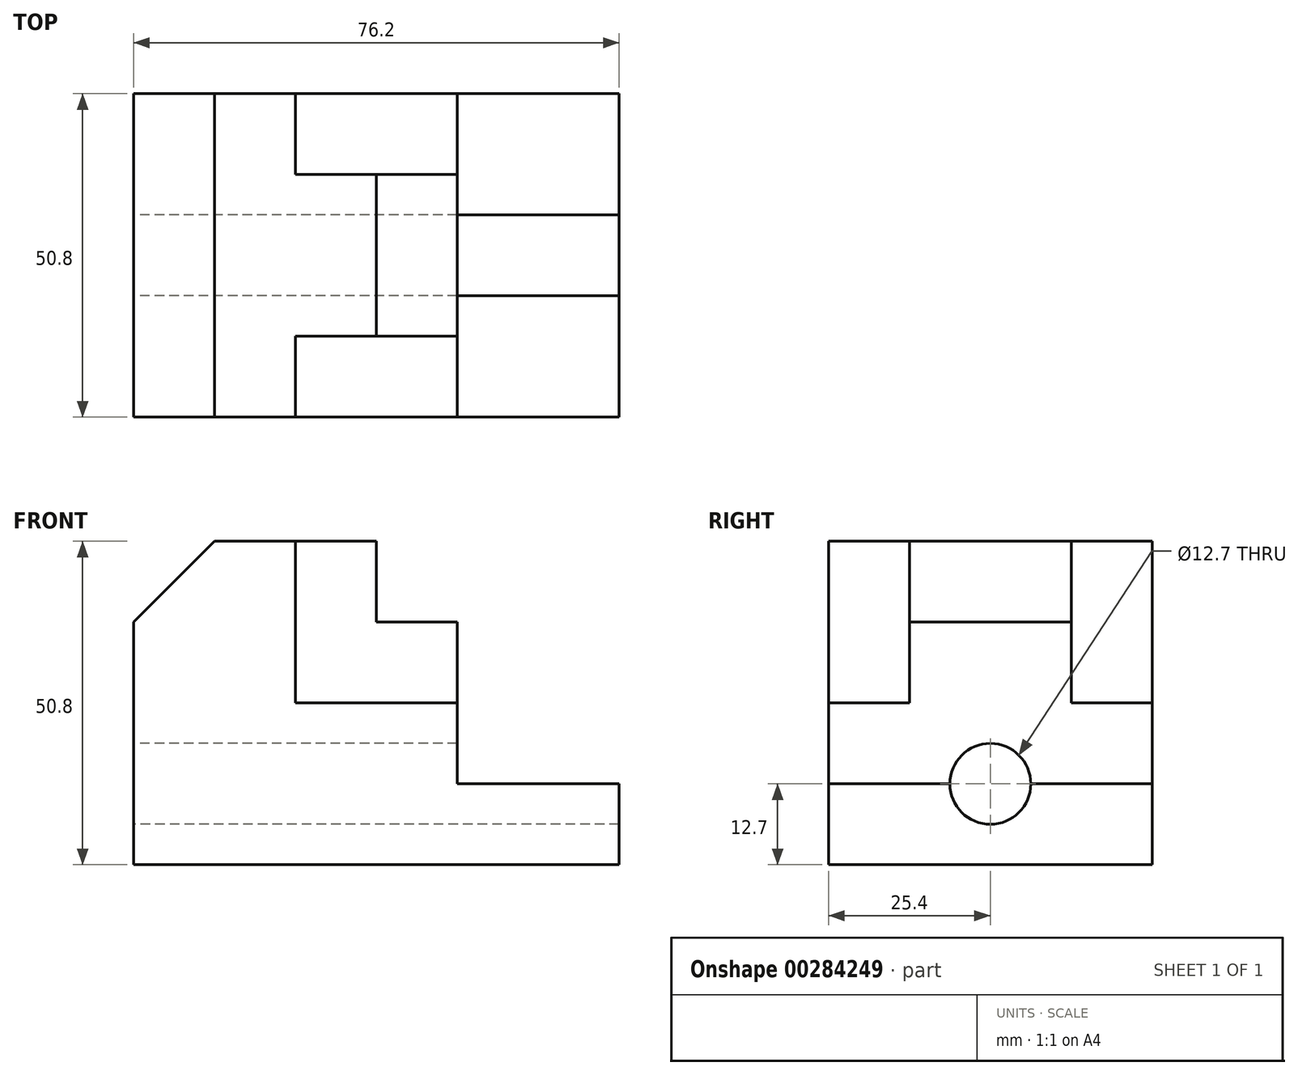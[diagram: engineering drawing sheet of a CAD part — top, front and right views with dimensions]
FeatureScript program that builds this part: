
annotation { "Feature Type Name" : "Feature", "Feature Type Description" : "" }
export const myFeature = defineFeature(function(context is Context, id is Id, definition is map)
    precondition{}
    {
        {
            var Q0;
            Q0=qCreatedBy(makeId("Front.planeOp"),FACE);
            var sketch = newSketch(context, id + "F0", { "sketchPlane" : qUnion([Q0])});
            skLineSegment(sketch, "E0.bottom", {"start": v(0, 0) * mm, "end": v(76.2, 0) * mm});
            skLineSegment(sketch, "E0.top", {"start": v(0, 12.7) * mm, "end": v(76.2, 12.7) * mm});
            skLineSegment(sketch, "E0.left", {"start": v(0, 0) * mm, "end": v(0, 12.7) * mm});
            skLineSegment(sketch, "E0.right", {"start": v(76.2, 0) * mm, "end": v(76.2, 12.7) * mm});
            skLineSegment(sketch, "E1.bottom", {"start": v(0, 12.7) * mm, "end": v(50.8, 12.7) * mm});
            skLineSegment(sketch, "E1.top", {"start": v(0, 25.4) * mm, "end": v(50.8, 25.4) * mm});
            skLineSegment(sketch, "E1.left", {"start": v(0, 12.7) * mm, "end": v(0, 25.4) * mm});
            skLineSegment(sketch, "E1.right", {"start": v(50.8, 12.7) * mm, "end": v(50.8, 25.4) * mm});
            skLineSegment(sketch, "E2", {"start": v(0, 25.4) * mm, "end": v(25.4, 25.4) * mm});
            skLineSegment(sketch, "E3", {"start": v(25.4, 25.4) * mm, "end": v(25.4, 50.8) * mm});
            skLineSegment(sketch, "E4", {"start": v(25.4, 50.8) * mm, "end": v(12.7, 50.8) * mm});
            skLineSegment(sketch, "E5", {"start": v(0, 25.4) * mm, "end": v(0, 38.1) * mm});
            skLineSegment(sketch, "E6", {"start": v(0, 38.1) * mm, "end": v(12.7, 50.8) * mm});
            skSolve(sketch);
        }
        {
            var Q0;
            Q0 = qSketchRegion(id + "F0", true);
            extrude(context, id + "F1", {"entities" : qUnion([Q0]), "endBound" : BoundingType.SYMMETRIC, "depth" : 50.8 * mm});
        }
        {
            var Q0;
            Q0=qCreatedBy(makeId("Right.planeOp"),FACE);
            var sketch = newSketch(context, id + "F2", { "sketchPlane" : qUnion([Q0])});
            skCircle(sketch, "E7", {"center": v(0, 12.7) * mm, "radius": 6.35 * mm});
            skSolve(sketch);
        }
        {
            var Q0;
            Q0 = qSketchRegion(id + "F2", true);
            extrude(context, id + "F3", {"entities" : qUnion([Q0]), "operationType" : NewBodyOperationType.REMOVE, "endBound" : BoundingType.THROUGH_ALL, "depth" : 25.4 * mm});
        }
        {
            var Q0;
            Q0=qCreatedBy(makeId("Front.planeOp"),FACE);
            var sketch = newSketch(context, id + "F4", { "sketchPlane" : qUnion([Q0])});
            skLineSegment(sketch, "E8", {"start": v(25.4, 50.8) * mm, "end": v(38.1, 50.8) * mm});
            skLineSegment(sketch, "E9", {"start": v(38.1, 50.8) * mm, "end": v(38.1, 38.1) * mm});
            skLineSegment(sketch, "E10", {"start": v(38.1, 38.1) * mm, "end": v(50.8, 38.1) * mm});
            skLineSegment(sketch, "E11", {"start": v(50.8, 38.1) * mm, "end": v(50.8, 25.4) * mm});
            skLineSegment(sketch, "E12", {"start": v(50.8, 25.4) * mm, "end": v(25.4, 25.4) * mm});
            skLineSegment(sketch, "E13", {"start": v(25.4, 25.4) * mm, "end": v(25.4, 50.8) * mm});
            skSolve(sketch);
        }
        {
            var Q0;
            Q0 = qSketchRegion(id + "F4", true);
            extrude(context, id + "F5", {"entities" : qUnion([Q0]), "operationType" : NewBodyOperationType.ADD, "endBound" : BoundingType.SYMMETRIC, "depth" : 25.4 * mm});
        }
    });
